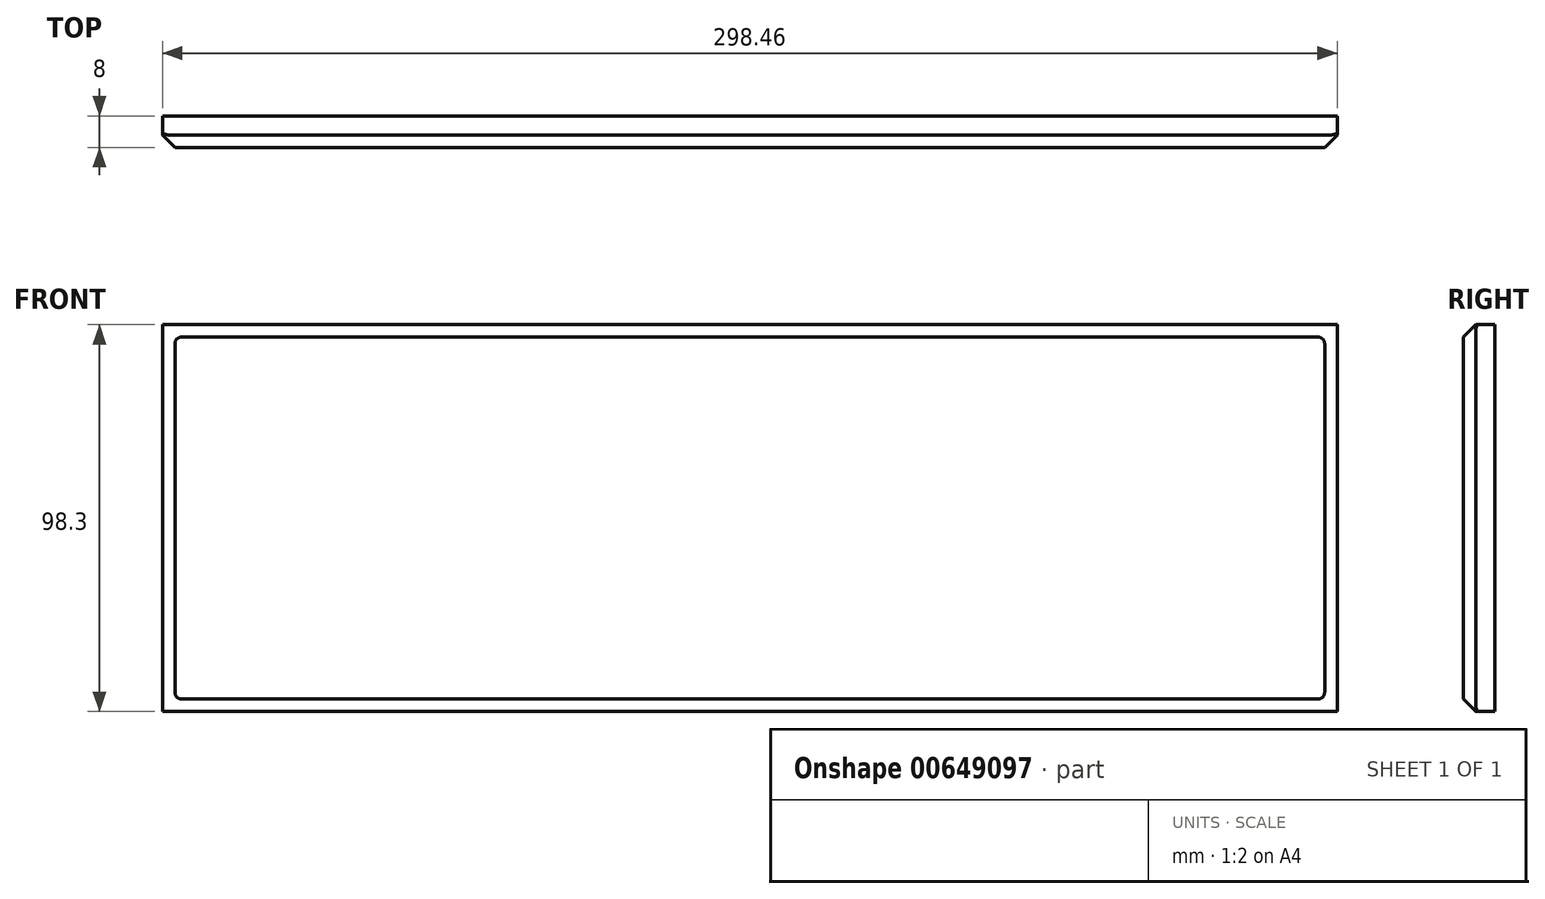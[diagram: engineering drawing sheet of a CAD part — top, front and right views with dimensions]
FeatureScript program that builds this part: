
annotation { "Feature Type Name" : "Feature", "Feature Type Description" : "" }
export const myFeature = defineFeature(function(context is Context, id is Id, definition is map)
    precondition{}
    {
        {
            var Q0;
            Q0=qCreatedBy(makeId("Front.planeOp"),FACE);
            var sketch = newSketch(context, id + "F0", { "sketchPlane" : qUnion([Q0])});
            skLineSegment(sketch, "E0.bottom", {"start": v(149.23, 49.15) * mm, "end": v(-149.23, 49.15) * mm});
            skLineSegment(sketch, "E0.top", {"start": v(149.23, -49.15) * mm, "end": v(-149.23, -49.15) * mm});
            skLineSegment(sketch, "E0.left", {"start": v(149.23, 49.15) * mm, "end": v(149.23, -49.15) * mm});
            skLineSegment(sketch, "E0.right", {"start": v(-149.23, 49.15) * mm, "end": v(-149.23, -49.15) * mm});
            skPoint(sketch, "E0.middle", {"position": v(0, 0) * mm});
            skSolve(sketch);
        }
        {
            var Q0;
            Q0=qSketchRegion(id+"F0",true);
            extrude(context, id + "F1", {"entities" : qUnion([Q0]), "depth" : 8 * mm, "offsetDistance" : 25.4 * mm});
        }
        {
            var Q0;
            Q0=makeQuery(id+"F1.opExtrude","CAP_EDGE",EDGE,{"disambiguationData":[OSD([sQuery(id+"F0.wireOp",EDGE,"E0.bottom")])],"isStart":false});
            var Q1;
            Q1=makeQuery(id+"F1.opExtrude","CAP_EDGE",EDGE,{"disambiguationData":[OSD([sQuery(id+"F0.wireOp",EDGE,"E0.right")])],"isStart":false});
            var Q2;
            Q2=makeQuery(id+"F1.opExtrude","CAP_EDGE",EDGE,{"disambiguationData":[OSD([sQuery(id+"F0.wireOp",EDGE,"E0.top")])],"isStart":false});
            var Q3;
            Q3=makeQuery(id+"F1.opExtrude","CAP_EDGE",EDGE,{"disambiguationData":[OSD([sQuery(id+"F0.wireOp",EDGE,"E0.left")])],"isStart":false});
            chamfer(context, id + "F2", {"entities" : qUnion([Q0, Q1, Q2, Q3]), "width" : 3.17 * mm, "tangentPropagation" : true});
        }
        {
            var Q0;
            Q0=makeQuery(id+"F2.opChamfer","BLEND_EDGE",EDGE,{"blendedFrom":[makeQuery(id+"F1.opExtrude","CAP_EDGE",EDGE,{"disambiguationData":[OSD([sQuery(id+"F0.wireOp",EDGE,"E0.bottom")])],"isStart":false}),makeQuery(id+"F1.opExtrude","CAP_EDGE",EDGE,{"disambiguationData":[OSD([sQuery(id+"F0.wireOp",EDGE,"E0.left")])],"isStart":false})],"blendedInto":[]});
            var Q1;
            Q1=makeQuery(id+"F2.opChamfer","BLEND_EDGE",EDGE,{"blendedFrom":[makeQuery(id+"F1.opExtrude","CAP_EDGE",EDGE,{"disambiguationData":[OSD([sQuery(id+"F0.wireOp",EDGE,"E0.top")])],"isStart":false}),makeQuery(id+"F1.opExtrude","CAP_EDGE",EDGE,{"disambiguationData":[OSD([sQuery(id+"F0.wireOp",EDGE,"E0.left")])],"isStart":false})],"blendedInto":[]});
            var Q2;
            Q2=makeQuery(id+"F2.opChamfer","BLEND_EDGE",EDGE,{"blendedFrom":[makeQuery(id+"F1.opExtrude","CAP_EDGE",EDGE,{"disambiguationData":[OSD([sQuery(id+"F0.wireOp",EDGE,"E0.top")])],"isStart":false}),makeQuery(id+"F1.opExtrude","CAP_EDGE",EDGE,{"disambiguationData":[OSD([sQuery(id+"F0.wireOp",EDGE,"E0.right")])],"isStart":false})],"blendedInto":[]});
            var Q3;
            Q3=makeQuery(id+"F2.opChamfer","BLEND_EDGE",EDGE,{"blendedFrom":[makeQuery(id+"F1.opExtrude","CAP_EDGE",EDGE,{"disambiguationData":[OSD([sQuery(id+"F0.wireOp",EDGE,"E0.bottom")])],"isStart":false}),makeQuery(id+"F1.opExtrude","CAP_EDGE",EDGE,{"disambiguationData":[OSD([sQuery(id+"F0.wireOp",EDGE,"E0.right")])],"isStart":false})],"blendedInto":[]});
            fillet(context, id + "F3", {"entities" : qUnion([Q0, Q1, Q2, Q3]), "radius" : 2.54 * mm, "tangentPropagation" : true, "allowEdgeOverflow" : false});
        }
    });
